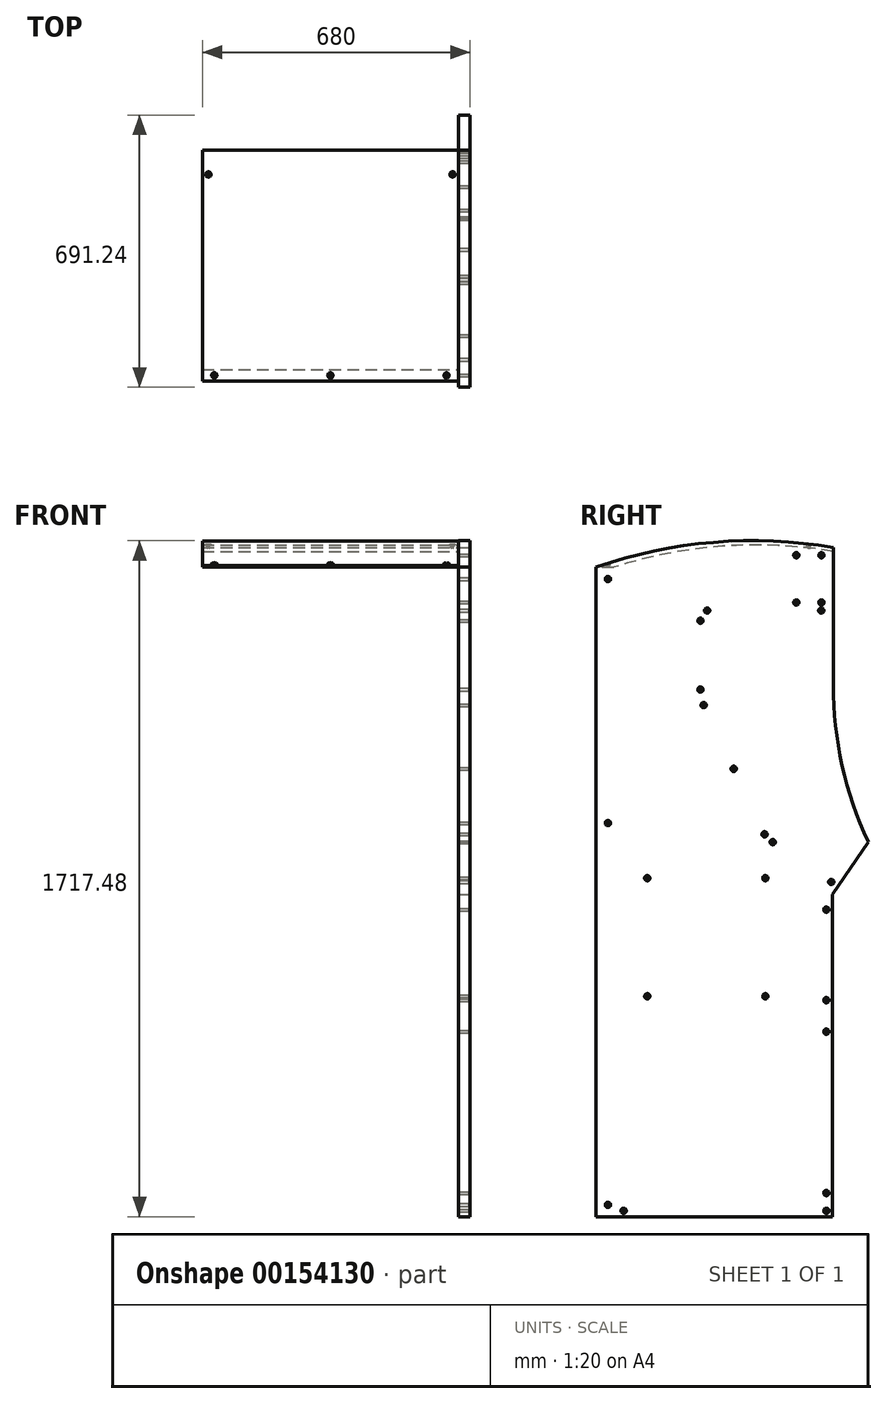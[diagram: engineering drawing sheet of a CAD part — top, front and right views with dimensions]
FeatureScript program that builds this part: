
annotation { "Feature Type Name" : "Feature", "Feature Type Description" : "" }
export const myFeature = defineFeature(function(context is Context, id is Id, definition is map)
    precondition{}
    {
        {
            var Q0;
            Q0=qCreatedBy(makeId("Right.planeOp"),FACE);
            var sketch = newSketch(context, id + "F0", { "sketchPlane" : qUnion([Q0])});
            skLineSegment(sketch, "E0", {"start": v(-279, -818.5) * mm, "end": v(-279, 831.5) * mm});
            skLineSegment(sketch, "E1", {"start": v(321, 0) * mm, "end": v(321, -818.5) * mm});
            skLineSegment(sketch, "E2", {"start": v(321, -818.5) * mm, "end": v(-279, -818.5) * mm});
            skArc(sketch, "E3", {"start": v(323.62, 881.5) * mm, "mid": v(19.13, 894.86) * mm, "end": v(-279, 831.5) * mm});
            skLineSegment(sketch, "E4", {"start": v(323.62, 881.5) * mm, "end": v(323.62, 532) * mm});
            skLineSegment(sketch, "E5", {"start": v(321, 0) * mm, "end": v(412.24, 134.02) * mm});
            skArc(sketch, "E6", {"start": v(323.62, 532) * mm, "mid": v(346.05, 328.14) * mm, "end": v(412.24, 134.02) * mm});
            skPoint(sketch, "E7", {"position": v(-249, -788.5) * mm});
            skPoint(sketch, "E8", {"position": v(306, -803.5) * mm});
            skPoint(sketch, "E9", {"position": v(306, -38.5) * mm});
            skPoint(sketch, "E10", {"position": v(293.62, 862) * mm});
            skPoint(sketch, "E11", {"position": v(293.62, 742) * mm});
            skPoint(sketch, "E12", {"position": v(-249, 801.5) * mm});
            skPoint(sketch, "E13", {"position": v(-249, 181.5) * mm});
            skPoint(sketch, "E14", {"position": v(318.52, 31.89) * mm});
            skPoint(sketch, "E15", {"position": v(229.62, 862) * mm});
            skPoint(sketch, "E16", {"position": v(229.62, 742) * mm});
            skPoint(sketch, "E17", {"position": v(306, -758.5) * mm});
            skPoint(sketch, "E18", {"position": v(306, -348.5) * mm});
            skPoint(sketch, "E19", {"position": v(-209, -803.5) * mm});
            skPoint(sketch, "E20", {"position": v(169.73, 133.19) * mm});
            skLineSegment(sketch, "E21", {"start": v(169.73, 133.19) * mm, "end": v(318.52, 31.89) * mm});
            skPoint(sketch, "E22", {"position": v(306, -268.5) * mm});
            skPoint(sketch, "E23", {"position": v(149.01, 152.93) * mm});
            skPoint(sketch, "E24", {"position": v(70.59, 319.38) * mm});
            skPoint(sketch, "E25", {"position": v(-5.7, 481.3) * mm});
            skLineSegment(sketch, "E26", {"start": v(-5.7, 481.3) * mm, "end": v(70.59, 319.38) * mm});
            skLineSegment(sketch, "E27", {"start": v(70.59, 319.38) * mm, "end": v(149.01, 152.93) * mm});
            skPoint(sketch, "E28", {"position": v(-14, 520.77) * mm});
            skPoint(sketch, "E29", {"position": v(-14, 695.77) * mm});
            skPoint(sketch, "E30", {"position": v(3.03, 721.42) * mm});
            skPoint(sketch, "E31", {"position": v(293.03, 721.42) * mm});
            skLineSegment(sketch, "E32", {"start": v(3.03, 721.42) * mm, "end": v(293.03, 721.42) * mm});
            skLineSegment(sketch, "E33.bottom", {"start": v(-149, -258.5) * mm, "end": v(151, -258.5) * mm});
            skLineSegment(sketch, "E33.top", {"start": v(-149, 41.5) * mm, "end": v(151, 41.5) * mm});
            skLineSegment(sketch, "E33.left", {"start": v(-149, -258.5) * mm, "end": v(-149, 41.5) * mm});
            skLineSegment(sketch, "E33.right", {"start": v(151, -258.5) * mm, "end": v(151, 41.5) * mm});
            skSolve(sketch);
        }
        {
            var Q0;
            Q0=makeQuery(id+"F0.imprint","IMPRINT",FACE,{"disambiguationData":[TD([[makeQuery(id+"F0.imprint","IMPRINT",EDGE,{"derivedFrom":sQuery(id+"F0.wireOp",EDGE,"E0")}),-1.0]])]});
            var Q1;
            Q1=makeQuery(id+"F0.imprint","IMPRINT",FACE,{"disambiguationData":[TD([[makeQuery(id+"F0.imprint","IMPRINT",EDGE,{"derivedFrom":sQuery(id+"F0.wireOp",EDGE,"E33.bottom")}),1.0]])]});
            extrude(context, id + "F1", {"entities" : qUnion([Q0, Q1]), "oppositeDirection" : true, "depth" : 30 * mm});
        }
        {
            var Q0;
            Q0=sQuery(id+"F0.wireOp",VERTEX,"b9837053-11db-4487-8885-cea22af114a3");
            var Q1;
            Q1=sQuery(id+"F0.wireOp",VERTEX,"E11");
            var Q2;
            Q2=sQuery(id+"F0.wireOp",VERTEX,"E10");
            var Q3;
            Q3=sQuery(id+"F0.wireOp",VERTEX,"E15");
            var Q4;
            Q4=sQuery(id+"F0.wireOp",VERTEX,"E16");
            var Q5;
            Q5=sQuery(id+"F0.wireOp",VERTEX,"E12");
            var Q6;
            Q6=sQuery(id+"F0.wireOp",VERTEX,"E13");
            var Q7;
            Q7=sQuery(id+"F0.wireOp",VERTEX,"E9");
            var Q8;
            Q8=sQuery(id+"F0.wireOp",VERTEX,"E18");
            var Q9;
            Q9=sQuery(id+"F0.wireOp",VERTEX,"E17");
            var Q10;
            Q10=sQuery(id+"F0.wireOp",VERTEX,"E8");
            var Q11;
            Q11=sQuery(id+"F0.wireOp",VERTEX,"E19");
            var Q12;
            Q12=sQuery(id+"F0.wireOp",VERTEX,"E7");
            var Q13;
            Q13=sQuery(id+"F0.wireOp",VERTEX,"E22");
            var Q14;
            Q14=sQuery(id+"F0.wireOp",VERTEX,"E14");
            var Q15;
            Q15=sQuery(id+"F0.wireOp",VERTEX,"E20");
            var Q16;
            Q16=sQuery(id+"F0.wireOp",VERTEX,"E23");
            var Q17;
            Q17=sQuery(id+"F0.wireOp",VERTEX,"E24");
            var Q18;
            Q18=sQuery(id+"F0.wireOp",VERTEX,"E25");
            var Q19;
            Q19=sQuery(id+"F0.wireOp",VERTEX,"E28");
            var Q20;
            Q20=sQuery(id+"F0.wireOp",VERTEX,"E29");
            var Q21;
            Q21=sQuery(id+"F0.wireOp",VERTEX,"E31");
            var Q22;
            Q22=sQuery(id+"F0.wireOp",VERTEX,"E30");
            var Q23;
            Q23=sQuery(id+"F0.wireOp",VERTEX,"E33.top.start");
            var Q24;
            Q24=sQuery(id+"F0.wireOp",VERTEX,"E33.top.end");
            var Q25;
            Q25=sQuery(id+"F0.wireOp",VERTEX,"E33.bottom.end");
            var Q26;
            Q26=sQuery(id+"F0.wireOp",VERTEX,"E33.left.start");
            var Q27;
            Q27=makeQuery(id+"F1.opExtrude","SWEPT_BODY",BODY,{"disambiguationData":[OSD([sQuery(id+"F0.wireOp",EDGE,"E0"),sQuery(id+"F0.wireOp",EDGE,"E1"),sQuery(id+"F0.wireOp",EDGE,"E2"),sQuery(id+"F0.wireOp",EDGE,"E3"),sQuery(id+"F0.wireOp",EDGE,"E4"),sQuery(id+"F0.wireOp",EDGE,"E5"),sQuery(id+"F0.wireOp",EDGE,"E6")])]});
            hole(context, id + "F2", {"style" : HoleStyle.C_SINK, "endStyle" : HoleEndStyle.THROUGH, "standardTappedOrClearance" : lookupTablePath({ "standard" : "ISO", "fit" : "Normal", "size" : "M6", "type" : "Clearance" }), "standardBlindInLast" : lookupTablePath({ "fit" : "Standard", "standard" : "ISO", "size" : "M6", "type" : "Clearance" }), "holeDiameter" : 6.6 * mm, "cSinkDiameter" : 13.44 * mm, "cSinkAngle" : 90 * degree, "locations" : qUnion([Q0, Q1, Q2, Q3, Q4, Q5, Q6, Q7, Q8, Q9, Q10, Q11, Q12, Q13, Q14, Q15, Q16, Q17, Q18, Q19, Q20, Q21, Q22, Q23, Q24, Q25, Q26]), "scope" : qUnion([Q27]), "isTappedThrough" : true});
        }
        {
            var Q0;
            Q0=makeQuery(id+"F1.opExtrude","CAP_FACE",FACE,{"disambiguationData":[OSD([sQuery(id+"F0.wireOp",EDGE,"E0"),sQuery(id+"F0.wireOp",EDGE,"E1"),sQuery(id+"F0.wireOp",EDGE,"E2"),sQuery(id+"F0.wireOp",EDGE,"E3"),sQuery(id+"F0.wireOp",EDGE,"E4"),sQuery(id+"F0.wireOp",EDGE,"E5"),sQuery(id+"F0.wireOp",EDGE,"E6")])],"isStart":false});
            var sketch = newSketch(context, id + "F3", { "sketchPlane" : qUnion([Q0])});
            skLineSegment(sketch, "E34", {"start": v(-323.62, 881.5) * mm, "end": v(-323.62, 872) * mm});
            skLineSegment(sketch, "E35", {"start": v(264, 831.5) * mm, "end": v(234, 831.5) * mm});
            skArc(sketch, "E36", {"start": v(234, 831.5) * mm, "mid": v(-42.4, 884.89) * mm, "end": v(-323.62, 872) * mm});
            skLineSegment(sketch, "E37", {"start": v(264, 831.5) * mm, "end": v(264, 836) * mm});
            skArc(sketch, "E38", {"start": v(264, 836) * mm, "mid": v(-27.1, 893.75) * mm, "end": v(-323.62, 881.5) * mm});
            skSolve(sketch);
        }
        {
            var Q0;
            Q0 = qSketchRegion(id + "F3", true);
            extrude(context, id + "F4", {"entities" : qUnion([Q0]), "depth" : 650 * mm});
        }
        {
            var Q0;
            Q0=qCreatedBy(makeId("Top.planeOp"),FACE);
            cPlane(context, id + "F5", {"entities" : qUnion([Q0]), "cplaneType" : CPlaneType.OFFSET, "offset" : 1000 * mm, "width" : 150 * mm, "height" : 150 * mm});
        }
        {
            var Q0;
            Q0=qCreatedBy(id+"F5.planeOp",FACE);
            var sketch = newSketch(context, id + "F6", { "sketchPlane" : qUnion([Q0])});
            skLineSegment(sketch, "E39.bottom", {"start": v(-680, 323.63) * mm, "end": v(-30, 323.63) * mm});
            skLineSegment(sketch, "E39.top", {"start": v(-680, -264) * mm, "end": v(-30, -264) * mm});
            skLineSegment(sketch, "E39.left", {"start": v(-680, 323.63) * mm, "end": v(-680, -264) * mm});
            skLineSegment(sketch, "E39.right", {"start": v(-30, 323.63) * mm, "end": v(-30, -264) * mm});
            skPoint(sketch, "E40", {"position": v(-650, -249) * mm});
            skPoint(sketch, "E41", {"position": v(-355, -249) * mm});
            skPoint(sketch, "E42", {"position": v(-60, -249) * mm});
            skPoint(sketch, "E43", {"position": v(-665, 261.63) * mm});
            skPoint(sketch, "E44", {"position": v(-45, 261.63) * mm});
            skSolve(sketch);
        }
        {
            var Q0;
            Q0=sQuery(id+"F6.wireOp",VERTEX,"E40");
            var Q1;
            Q1=sQuery(id+"F6.wireOp",VERTEX,"E41");
            var Q2;
            Q2=sQuery(id+"F6.wireOp",VERTEX,"E42");
            var Q3;
            Q3=sQuery(id+"F6.wireOp",VERTEX,"E43");
            var Q4;
            Q4=sQuery(id+"F6.wireOp",VERTEX,"E44");
            var Q5;
            Q5=makeQuery(id+"F4.opExtrude","SWEPT_BODY",BODY,{"disambiguationData":[OSD([sQuery(id+"F3.wireOp",EDGE,"E34"),sQuery(id+"F3.wireOp",EDGE,"E35"),sQuery(id+"F3.wireOp",EDGE,"E36"),sQuery(id+"F3.wireOp",EDGE,"E37"),sQuery(id+"F3.wireOp",EDGE,"E38")])]});
            hole(context, id + "F7", {"style" : HoleStyle.C_SINK, "endStyle" : HoleEndStyle.THROUGH, "standardTappedOrClearance" : lookupTablePath({ "standard" : "ISO", "fit" : "Normal", "size" : "M6", "type" : "Clearance" }), "standardBlindInLast" : lookupTablePath({ "fit" : "Standard", "standard" : "ISO", "size" : "M6", "type" : "Clearance" }), "holeDiameter" : 6.6 * mm, "cSinkDiameter" : 13.44 * mm, "cSinkAngle" : 90 * degree, "locations" : qUnion([Q0, Q1, Q2, Q3, Q4]), "scope" : qUnion([Q5]), "isTappedThrough" : true});
        }
    });
